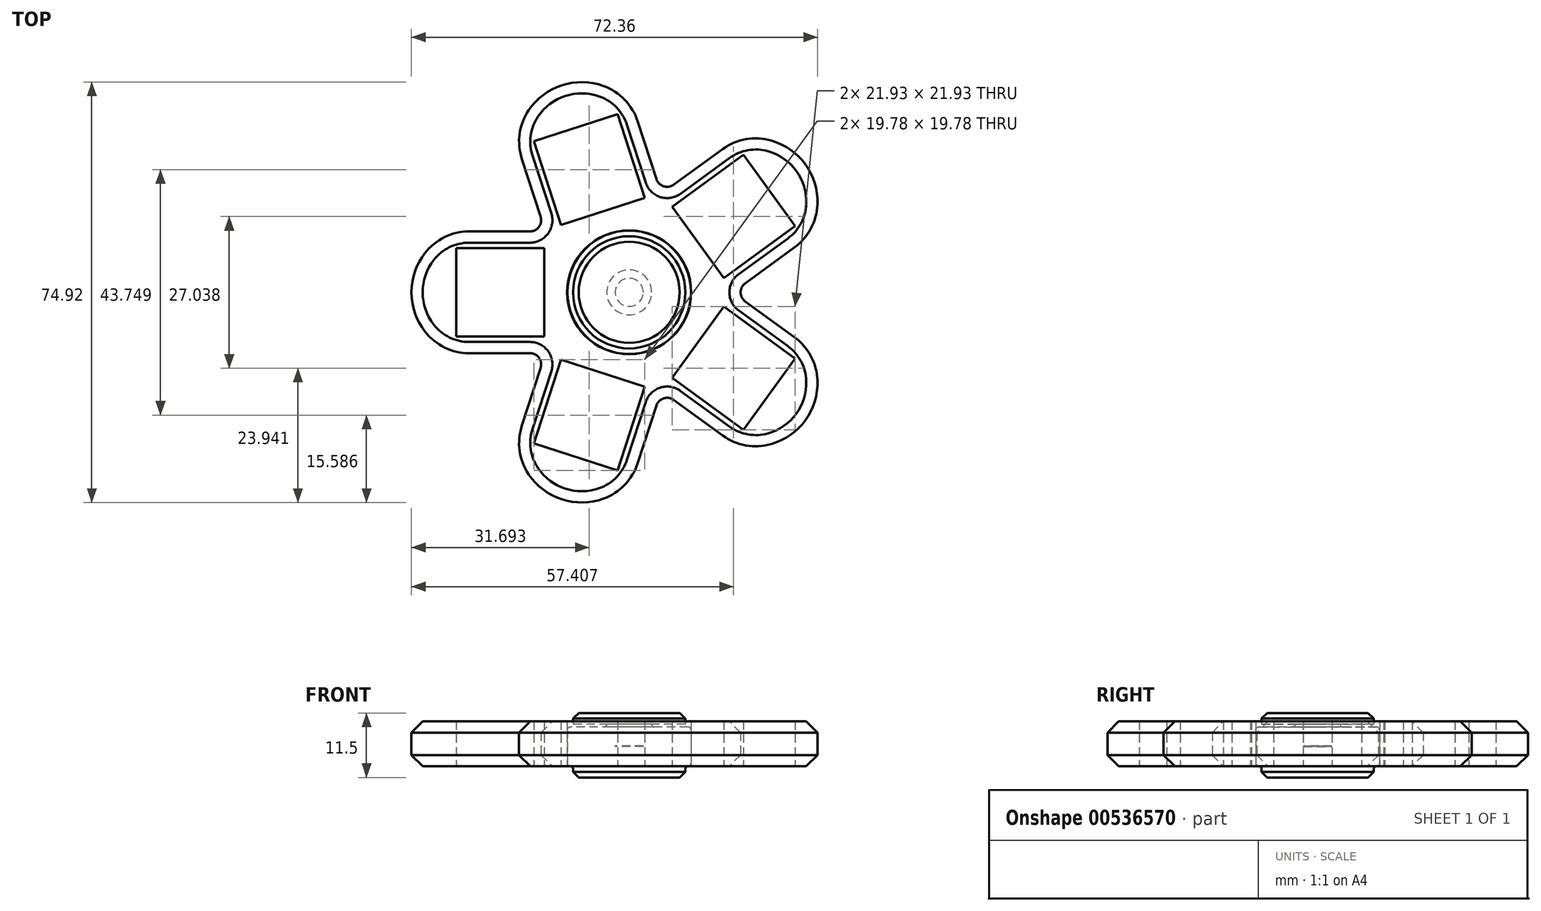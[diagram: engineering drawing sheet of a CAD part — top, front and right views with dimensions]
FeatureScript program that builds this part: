
annotation { "Feature Type Name" : "Feature", "Feature Type Description" : "" }
export const myFeature = defineFeature(function(context is Context, id is Id, definition is map)
    precondition{}
    {
        {
            var Q0;
            Q0=qCreatedBy(makeId("Top.planeOp"),FACE);
            var sketch = newSketch(context, id + "F0", { "sketchPlane" : qUnion([Q0])});
            skCircle(sketch, "E0", {"center": v(0, 0) * mm, "radius": 11 * mm});
            skCircle(sketch, "E1", {"center": v(0, 0) * mm, "radius": 4 * mm});
            skSolve(sketch);
        }
        {
            var Q0;
            Q0=makeQuery(id+"F0.imprint","IMPRINT",FACE,{"disambiguationData":[TD([[makeQuery(id+"F0.imprint","IMPRINT",EDGE,{"derivedFrom":sQuery(id+"F0.wireOp",EDGE,"E0")}),1.0]])]});
            extrude(context, id + "F1", {"entities" : qUnion([Q0]), "depth" : 7 * mm, "offsetDistance" : 25 * mm});
        }
        {
            var Q0;
            Q0=makeQuery(id+"F1.opExtrude","CAP_FACE",FACE,{"disambiguationData":[OSD([sQuery(id+"F0.wireOp",EDGE,"E0"),sQuery(id+"F0.wireOp",EDGE,"E1")])],"isStart":true});
            var sketch = newSketch(context, id + "F2", { "sketchPlane" : qUnion([Q0])});
            skCircle(sketch, "E2.0", {"center": v(0, 0) * mm, "radius": 11.05 * mm});
            skCircle(sketch, "E3.0", {"center": v(0, 0) * mm, "radius": 15.05 * mm});
            skLineSegment(sketch, "E4", {"start": v(0, 0) * mm, "end": v(-23, 0) * mm, "construction": true});
            skLineSegment(sketch, "E5.bottom", {"start": v(-30.85, -7.85) * mm, "end": v(-15.15, -7.85) * mm});
            skLineSegment(sketch, "E5.top", {"start": v(-30.85, 7.85) * mm, "end": v(-15.15, 7.85) * mm});
            skLineSegment(sketch, "E5.left", {"start": v(-30.85, -7.85) * mm, "end": v(-30.85, 7.85) * mm});
            skLineSegment(sketch, "E5.right", {"start": v(-15.15, -7.85) * mm, "end": v(-15.15, 7.85) * mm});
            skPoint(sketch, "E5.middle", {"position": v(-23, 0) * mm});
            skCircle(sketch, "E6", {"center": v(0, 0) * mm, "radius": 50 * mm, "construction": true});
            skLineSegment(sketch, "E7", {"start": v(-23, 0) * mm, "end": v(-38.8, 0) * mm, "construction": true});
            skLineSegment(sketch, "E8", {"start": v(-30.85, 7.85) * mm, "end": v(-30.85, 10.85) * mm, "construction": true});
            skLineSegment(sketch, "E9.0", {"start": v(-23, 10.85) * mm, "end": v(-30.85, 10.85) * mm});
            skLineSegment(sketch, "E9.1", {"start": v(0, 10.85) * mm, "end": v(-2.1, 10.85) * mm, "construction": true});
            skLineSegment(sketch, "E10.trimOffspring", {"start": v(-10.43, 10.85) * mm, "end": v(-23, 10.85) * mm});
            skLineSegment(sketch, "E11.MirrorCS", {"start": v(-10.43, -10.85) * mm, "end": v(-23, -10.85) * mm});
            skLineSegment(sketch, "E12.MirrorCS", {"start": v(-23, -10.85) * mm, "end": v(-30.85, -10.85) * mm});
            skArc(sketch, "E13", {"start": v(-30.85, 10.85) * mm, "mid": v(-38.8, 0) * mm, "end": v(-30.85, -10.85) * mm});
            skLineSegment(sketch, "E14.1.0", {"start": v(-2.07, -31.77) * mm, "end": v(2.78, -16.83) * mm});
            skLineSegment(sketch, "E14.1.1", {"start": v(2.78, -16.83) * mm, "end": v(-12.15, -11.98) * mm});
            skLineSegment(sketch, "E14.1.2", {"start": v(-17, -26.91) * mm, "end": v(-12.15, -11.98) * mm});
            skLineSegment(sketch, "E14.1.3", {"start": v(-13.54, -6.57) * mm, "end": v(-17.43, -18.52) * mm});
            skLineSegment(sketch, "E14.1.4", {"start": v(-17.43, -18.52) * mm, "end": v(-19.85, -25.99) * mm});
            skLineSegment(sketch, "E14.1.5", {"start": v(-2.07, -31.77) * mm, "end": v(-17, -26.91) * mm});
            skArc(sketch, "E14.1.6", {"start": v(-19.85, -25.99) * mm, "mid": v(-11.99, -36.9) * mm, "end": v(0.79, -32.7) * mm});
            skLineSegment(sketch, "E14.1.7", {"start": v(3.21, -25.23) * mm, "end": v(0.79, -32.7) * mm});
            skLineSegment(sketch, "E14.1.8", {"start": v(7.1, -13.27) * mm, "end": v(3.21, -25.23) * mm});
            skLineSegment(sketch, "E14.2.0", {"start": v(29.57, -11.78) * mm, "end": v(16.87, -2.55) * mm});
            skLineSegment(sketch, "E14.2.1", {"start": v(16.87, -2.55) * mm, "end": v(7.64, -15.26) * mm});
            skLineSegment(sketch, "E14.2.2", {"start": v(20.34, -24.48) * mm, "end": v(7.64, -15.26) * mm});
            skLineSegment(sketch, "E14.2.3", {"start": v(2.06, -14.9) * mm, "end": v(12.23, -22.3) * mm});
            skLineSegment(sketch, "E14.2.4", {"start": v(12.23, -22.3) * mm, "end": v(18.58, -26.91) * mm});
            skLineSegment(sketch, "E14.2.5", {"start": v(29.57, -11.78) * mm, "end": v(20.34, -24.48) * mm});
            skArc(sketch, "E14.2.6", {"start": v(18.58, -26.91) * mm, "mid": v(31.39, -22.8) * mm, "end": v(31.34, -9.36) * mm});
            skLineSegment(sketch, "E14.2.7", {"start": v(24.98, -4.74) * mm, "end": v(31.34, -9.36) * mm});
            skLineSegment(sketch, "E14.2.8", {"start": v(14.82, 2.65) * mm, "end": v(24.98, -4.74) * mm});
            skCircle(sketch, "E15", {"center": v(0, 0) * mm, "radius": 32.7 * mm, "construction": true});
            skLineSegment(sketch, "E16.3.3.0", {"start": v(7.64, 15.26) * mm, "end": v(16.87, 2.55) * mm});
            skLineSegment(sketch, "E16.6.3.0", {"start": v(29.57, 11.78) * mm, "end": v(16.87, 2.55) * mm});
            skLineSegment(sketch, "E16.9.3.0", {"start": v(14.82, -2.65) * mm, "end": v(24.98, 4.74) * mm});
            skLineSegment(sketch, "E16.12.3.0", {"start": v(24.98, 4.74) * mm, "end": v(31.34, 9.36) * mm});
            skLineSegment(sketch, "E16.15.3.0", {"start": v(20.34, 24.48) * mm, "end": v(29.57, 11.78) * mm});
            skArc(sketch, "E16.18.3.0", {"start": v(31.34, 9.36) * mm, "mid": v(31.39, 22.8) * mm, "end": v(18.58, 26.91) * mm});
            skLineSegment(sketch, "E16.21.3.0", {"start": v(20.34, 24.48) * mm, "end": v(7.64, 15.26) * mm});
            skLineSegment(sketch, "E16.22.3.0", {"start": v(12.23, 22.3) * mm, "end": v(18.58, 26.91) * mm});
            skLineSegment(sketch, "E16.25.3.0", {"start": v(2.06, 14.9) * mm, "end": v(12.23, 22.3) * mm});
            skLineSegment(sketch, "E16.3.4.0", {"start": v(-12.15, 11.98) * mm, "end": v(2.78, 16.83) * mm});
            skLineSegment(sketch, "E16.6.4.0", {"start": v(-2.07, 31.77) * mm, "end": v(2.78, 16.83) * mm});
            skLineSegment(sketch, "E16.9.4.0", {"start": v(7.1, 13.27) * mm, "end": v(3.21, 25.23) * mm});
            skLineSegment(sketch, "E16.12.4.0", {"start": v(3.21, 25.23) * mm, "end": v(0.79, 32.7) * mm});
            skLineSegment(sketch, "E16.15.4.0", {"start": v(-17, 26.91) * mm, "end": v(-2.07, 31.77) * mm});
            skArc(sketch, "E16.18.4.0", {"start": v(0.79, 32.7) * mm, "mid": v(-11.99, 36.9) * mm, "end": v(-19.85, 25.99) * mm});
            skLineSegment(sketch, "E16.21.4.0", {"start": v(-17, 26.91) * mm, "end": v(-12.15, 11.98) * mm});
            skLineSegment(sketch, "E16.22.4.0", {"start": v(-17.43, 18.52) * mm, "end": v(-19.85, 25.99) * mm});
            skLineSegment(sketch, "E16.25.4.0", {"start": v(-13.54, 6.57) * mm, "end": v(-17.43, 18.52) * mm});
            skSolve(sketch);
        }
        {
            var Q0;
            {var subQ5=sQuery(id+"F2.wireOp",EDGE,"E14.2.0");Q0=makeQuery(id+"F2.imprint","IMPRINT",FACE,{"disambiguationData":[TD([[makeQuery(id+"F2.imprint","IMPRINT",EDGE,{"derivedFrom":subQ5}),-1.0]])]});}
            var Q1;
            {var subQ6=sQuery(id+"F2.wireOp",EDGE,"E14.1.0");Q1=makeQuery(id+"F2.imprint","IMPRINT",FACE,{"disambiguationData":[TD([[makeQuery(id+"F2.imprint","IMPRINT",EDGE,{"derivedFrom":subQ6}),-1.0]])]});}
            var Q2;
            {var subQ5=sQuery(id+"F2.wireOp",EDGE,"E5.bottom");Q2=makeQuery(id+"F2.imprint","IMPRINT",FACE,{"disambiguationData":[TD([[makeQuery(id+"F2.imprint","IMPRINT",EDGE,{"derivedFrom":subQ5}),-1.0]])]});}
            var Q3;
            Q3=makeQuery(id+"F2.imprint","IMPRINT",FACE,{"disambiguationData":[TD([[makeQuery(id+"F2.imprint","IMPRINT",EDGE,{"derivedFrom":sQuery(id+"F2.wireOp",EDGE,"E16.3.4.0")}),-1.0]])]});
            var Q4;
            {var subQ0=sQuery(id+"F2.wireOp",EDGE,"E10.trimOffspring");var subQ1=sQuery(id+"F2.wireOp",EDGE,"E3.0");var subQ2=makeQuery(id+"F2.imprint","INTERSECT",VERTEX,{"derivedFrom":[subQ1,subQ0]});Q4=makeQuery(id+"F2.imprint","IMPRINT",FACE,{"disambiguationData":[TD([[makeQuery(id+"F2.imprint","IMPRINT",EDGE,{"disambiguationData":[TD([[subQ2,-1.0]])],"derivedFrom":subQ1}),-1.0]])]});}
            var Q5;
            Q5=makeQuery(id+"F2.imprint","IMPRINT",FACE,{"disambiguationData":[TD([[makeQuery(id+"F2.imprint","IMPRINT",EDGE,{"derivedFrom":sQuery(id+"F2.wireOp",EDGE,"E16.3.3.0")}),-1.0]])]});
            var Q6;
            {var subQ0=sQuery(id+"F2.wireOp",EDGE,"E16.25.3.0");var subQ1=sQuery(id+"F2.wireOp",EDGE,"E3.0");var subQ2=makeQuery(id+"F2.imprint","INTERSECT",VERTEX,{"derivedFrom":[subQ1,subQ0]});Q6=makeQuery(id+"F2.imprint","IMPRINT",FACE,{"disambiguationData":[TD([[makeQuery(id+"F2.imprint","IMPRINT",EDGE,{"disambiguationData":[TD([[subQ2,1.0]])],"derivedFrom":subQ1}),-1.0]])]});}
            var Q7;
            {var subQ0=sQuery(id+"F2.wireOp",EDGE,"E14.2.8");var subQ1=sQuery(id+"F2.wireOp",EDGE,"E3.0");var subQ2=makeQuery(id+"F2.imprint","INTERSECT",VERTEX,{"derivedFrom":[subQ1,subQ0]});Q7=makeQuery(id+"F2.imprint","IMPRINT",FACE,{"disambiguationData":[TD([[makeQuery(id+"F2.imprint","IMPRINT",EDGE,{"disambiguationData":[TD([[subQ2,1.0]])],"derivedFrom":subQ1}),-1.0]])]});}
            var Q8;
            {var subQ0=sQuery(id+"F2.wireOp",EDGE,"E11.MirrorCS");var subQ1=sQuery(id+"F2.wireOp",EDGE,"E3.0");var subQ2=makeQuery(id+"F2.imprint","INTERSECT",VERTEX,{"derivedFrom":[subQ1,subQ0]});Q8=makeQuery(id+"F2.imprint","IMPRINT",FACE,{"disambiguationData":[TD([[makeQuery(id+"F2.imprint","IMPRINT",EDGE,{"disambiguationData":[TD([[subQ2,1.0]])],"derivedFrom":subQ1}),-1.0]])]});}
            var Q9;
            Q9=makeQuery(id+"F2.imprint","IMPRINT",FACE,{"disambiguationData":[TD([[makeQuery(id+"F2.imprint","IMPRINT",EDGE,{"derivedFrom":sQuery(id+"F2.wireOp",EDGE,"E2.0")}),-1.0]])]});
            var Q10;
            {var subQ0=sQuery(id+"F2.wireOp",EDGE,"E14.1.8");var subQ1=sQuery(id+"F2.wireOp",EDGE,"E3.0");var subQ2=makeQuery(id+"F2.imprint","INTERSECT",VERTEX,{"derivedFrom":[subQ1,subQ0]});Q10=makeQuery(id+"F2.imprint","IMPRINT",FACE,{"disambiguationData":[TD([[makeQuery(id+"F2.imprint","IMPRINT",EDGE,{"disambiguationData":[TD([[subQ2,1.0]])],"derivedFrom":subQ1}),-1.0]])]});}
            extrude(context, id + "F3", {"entities" : qUnion([Q0, Q1, Q2, Q3, Q4, Q5, Q6, Q7, Q8, Q9, Q10]), "oppositeDirection" : true, "depth" : 8 * mm, "offsetDistance" : 25 * mm});
        }
        {
            var Q0;
            Q0=makeQuery(id+"F3.opExtrude","SWEPT_EDGE",EDGE,{"disambiguationData":[OSD([sQuery(id+"F2.wireOp",EDGE,"E3.0"),sQuery(id+"F2.wireOp",EDGE,"E14.2.3")])]});
            var Q1;
            Q1=makeQuery(id+"F3.opExtrude","SWEPT_EDGE",EDGE,{"disambiguationData":[OSD([sQuery(id+"F2.wireOp",EDGE,"E3.0"),sQuery(id+"F2.wireOp",EDGE,"E14.1.8")])]});
            var Q2;
            Q2=makeQuery(id+"F3.opExtrude","SWEPT_EDGE",EDGE,{"disambiguationData":[OSD([sQuery(id+"F2.wireOp",EDGE,"E3.0"),sQuery(id+"F2.wireOp",EDGE,"E14.2.8")])]});
            var Q3;
            Q3=makeQuery(id+"F3.opExtrude","SWEPT_EDGE",EDGE,{"disambiguationData":[OSD([sQuery(id+"F2.wireOp",EDGE,"E3.0"),sQuery(id+"F2.wireOp",EDGE,"E10.trimOffspring")])]});
            var Q4;
            Q4=makeQuery(id+"F3.opExtrude","SWEPT_EDGE",EDGE,{"disambiguationData":[OSD([sQuery(id+"F2.wireOp",EDGE,"E3.0"),sQuery(id+"F2.wireOp",EDGE,"E11.MirrorCS")])]});
            var Q5;
            Q5=makeQuery(id+"F3.opExtrude","SWEPT_EDGE",EDGE,{"disambiguationData":[OSD([sQuery(id+"F2.wireOp",EDGE,"E3.0"),sQuery(id+"F2.wireOp",EDGE,"E14.1.3")])]});
            var Q6;
            Q6=makeQuery(id+"F3.opExtrude","SWEPT_EDGE",EDGE,{"disambiguationData":[OSD([sQuery(id+"F2.wireOp",EDGE,"E16.25.3.0"),sQuery(id+"F2.wireOp",EDGE,"E16.9.4.0")])]});
            fillet(context, id + "F4", {"entities" : qUnion([Q0, Q1, Q2, Q3, Q4, Q5, Q6]), "radius" : 2 * mm, "tangentPropagation" : true, "allowEdgeOverflow" : false});
        }
        {
            var Q0;
            Q0=makeQuery(id+"F3.opExtrude","SWEPT_EDGE",EDGE,{"disambiguationData":[OSD([sQuery(id+"F2.wireOp",EDGE,"E14.2.4"),sQuery(id+"F2.wireOp",EDGE,"E14.2.6")])]});
            var Q1;
            Q1=makeQuery(id+"F3.opExtrude","SWEPT_EDGE",EDGE,{"disambiguationData":[OSD([sQuery(id+"F2.wireOp",EDGE,"E14.2.6"),sQuery(id+"F2.wireOp",EDGE,"E14.2.7")])]});
            var Q2;
            Q2=makeQuery(id+"F3.opExtrude","SWEPT_EDGE",EDGE,{"disambiguationData":[OSD([sQuery(id+"F2.wireOp",EDGE,"E9.0"),sQuery(id+"F2.wireOp",EDGE,"E13")])]});
            var Q3;
            Q3=makeQuery(id+"F3.opExtrude","SWEPT_EDGE",EDGE,{"disambiguationData":[OSD([sQuery(id+"F2.wireOp",EDGE,"E12.MirrorCS"),sQuery(id+"F2.wireOp",EDGE,"E13")])]});
            var Q4;
            Q4=makeQuery(id+"F3.opExtrude","SWEPT_EDGE",EDGE,{"disambiguationData":[OSD([sQuery(id+"F2.wireOp",EDGE,"E14.1.4"),sQuery(id+"F2.wireOp",EDGE,"E14.1.6")])]});
            var Q5;
            Q5=makeQuery(id+"F3.opExtrude","SWEPT_EDGE",EDGE,{"disambiguationData":[OSD([sQuery(id+"F2.wireOp",EDGE,"E14.1.6"),sQuery(id+"F2.wireOp",EDGE,"E14.1.7")])]});
            var Q6;
            Q6=makeQuery(id+"F3.opExtrude","SWEPT_EDGE",EDGE,{"disambiguationData":[OSD([sQuery(id+"F2.wireOp",EDGE,"E16.18.4.0"),sQuery(id+"F2.wireOp",EDGE,"E16.22.4.0")])]});
            var Q7;
            Q7=makeQuery(id+"F3.opExtrude","SWEPT_EDGE",EDGE,{"disambiguationData":[OSD([sQuery(id+"F2.wireOp",EDGE,"E16.12.4.0"),sQuery(id+"F2.wireOp",EDGE,"E16.18.4.0")])]});
            var Q8;
            Q8=makeQuery(id+"F3.opExtrude","SWEPT_EDGE",EDGE,{"disambiguationData":[OSD([sQuery(id+"F2.wireOp",EDGE,"E16.18.3.0"),sQuery(id+"F2.wireOp",EDGE,"E16.22.3.0")])]});
            var Q9;
            Q9=makeQuery(id+"F3.opExtrude","SWEPT_EDGE",EDGE,{"disambiguationData":[OSD([sQuery(id+"F2.wireOp",EDGE,"E16.12.3.0"),sQuery(id+"F2.wireOp",EDGE,"E16.18.3.0")])]});
            fillet(context, id + "F5", {"entities" : qUnion([Q0, Q1, Q2, Q3, Q4, Q5, Q6, Q7, Q8, Q9]), "radius" : 10 * mm, "tangentPropagation" : true, "allowEdgeOverflow" : false});
        }
        {
            var Q0;
            Q0=makeQuery(id+"F3.opExtrude","CAP_EDGE",EDGE,{"disambiguationData":[OSD([sQuery(id+"F2.wireOp",EDGE,"E14.2.6")])],"isStart":false});
            var Q1;
            Q1=makeQuery(id+"F3.opExtrude","CAP_EDGE",EDGE,{"disambiguationData":[OSD([sQuery(id+"F2.wireOp",EDGE,"E14.1.6")])],"isStart":false});
            var Q2;
            {var subQ0=sQuery(id+"F2.wireOp",EDGE,"E13");var subQ1=sQuery(id+"F2.wireOp",EDGE,"E9.0");Q2=makeQuery(id+"F5.opFillet","BLEND_EDGE",EDGE,{"blendedFrom":[makeQuery(id+"F3.opExtrude","SWEPT_EDGE",EDGE,{"disambiguationData":[OSD([subQ1,subQ0])]}),makeQuery(id+"F3.opExtrude","CAP_FACE",FACE,{"disambiguationData":[OSD([sQuery(id+"F2.wireOp",EDGE,"E2.0"),sQuery(id+"F2.wireOp",EDGE,"E3.0"),sQuery(id+"F2.wireOp",EDGE,"E5.bottom"),sQuery(id+"F2.wireOp",EDGE,"E5.top"),sQuery(id+"F2.wireOp",EDGE,"E5.left"),sQuery(id+"F2.wireOp",EDGE,"E5.right"),subQ1,sQuery(id+"F2.wireOp",EDGE,"E10.trimOffspring"),sQuery(id+"F2.wireOp",EDGE,"E11.MirrorCS"),sQuery(id+"F2.wireOp",EDGE,"E12.MirrorCS"),subQ0,sQuery(id+"F2.wireOp",EDGE,"E14.1.0"),sQuery(id+"F2.wireOp",EDGE,"E14.1.1"),sQuery(id+"F2.wireOp",EDGE,"E14.1.2"),sQuery(id+"F2.wireOp",EDGE,"E14.1.3"),sQuery(id+"F2.wireOp",EDGE,"E14.1.4"),sQuery(id+"F2.wireOp",EDGE,"E14.1.5"),sQuery(id+"F2.wireOp",EDGE,"E14.1.6"),sQuery(id+"F2.wireOp",EDGE,"E14.1.7"),sQuery(id+"F2.wireOp",EDGE,"E14.1.8"),sQuery(id+"F2.wireOp",EDGE,"E14.2.0"),sQuery(id+"F2.wireOp",EDGE,"E14.2.1"),sQuery(id+"F2.wireOp",EDGE,"E14.2.2"),sQuery(id+"F2.wireOp",EDGE,"E14.2.3"),sQuery(id+"F2.wireOp",EDGE,"E14.2.4"),sQuery(id+"F2.wireOp",EDGE,"E14.2.5"),sQuery(id+"F2.wireOp",EDGE,"E14.2.6"),sQuery(id+"F2.wireOp",EDGE,"E14.2.7"),sQuery(id+"F2.wireOp",EDGE,"E14.2.8")])],"isStart":false})],"blendedInto":[makeQuery(id+"F3.opExtrude","CAP_FACE",FACE,{"disambiguationData":[OSD([sQuery(id+"F2.wireOp",EDGE,"E2.0"),sQuery(id+"F2.wireOp",EDGE,"E3.0"),sQuery(id+"F2.wireOp",EDGE,"E5.bottom"),sQuery(id+"F2.wireOp",EDGE,"E5.top"),sQuery(id+"F2.wireOp",EDGE,"E5.left"),sQuery(id+"F2.wireOp",EDGE,"E5.right"),subQ1,sQuery(id+"F2.wireOp",EDGE,"E10.trimOffspring"),sQuery(id+"F2.wireOp",EDGE,"E11.MirrorCS"),sQuery(id+"F2.wireOp",EDGE,"E12.MirrorCS"),subQ0,sQuery(id+"F2.wireOp",EDGE,"E14.1.0"),sQuery(id+"F2.wireOp",EDGE,"E14.1.1"),sQuery(id+"F2.wireOp",EDGE,"E14.1.2"),sQuery(id+"F2.wireOp",EDGE,"E14.1.3"),sQuery(id+"F2.wireOp",EDGE,"E14.1.4"),sQuery(id+"F2.wireOp",EDGE,"E14.1.5"),sQuery(id+"F2.wireOp",EDGE,"E14.1.6"),sQuery(id+"F2.wireOp",EDGE,"E14.1.7"),sQuery(id+"F2.wireOp",EDGE,"E14.1.8"),sQuery(id+"F2.wireOp",EDGE,"E14.2.0"),sQuery(id+"F2.wireOp",EDGE,"E14.2.1"),sQuery(id+"F2.wireOp",EDGE,"E14.2.2"),sQuery(id+"F2.wireOp",EDGE,"E14.2.3"),sQuery(id+"F2.wireOp",EDGE,"E14.2.4"),sQuery(id+"F2.wireOp",EDGE,"E14.2.5"),sQuery(id+"F2.wireOp",EDGE,"E14.2.6"),sQuery(id+"F2.wireOp",EDGE,"E14.2.7"),sQuery(id+"F2.wireOp",EDGE,"E14.2.8")])],"isStart":false})]});}
            var Q3;
            Q3=makeQuery(id+"F3.opExtrude","CAP_EDGE",EDGE,{"disambiguationData":[OSD([sQuery(id+"F2.wireOp",EDGE,"E14.2.6")])],"isStart":true});
            var Q4;
            Q4=makeQuery(id+"F3.opExtrude","CAP_EDGE",EDGE,{"disambiguationData":[OSD([sQuery(id+"F2.wireOp",EDGE,"E13")])],"isStart":true});
            var Q5;
            Q5=makeQuery(id+"F3.opExtrude","CAP_EDGE",EDGE,{"disambiguationData":[OSD([sQuery(id+"F2.wireOp",EDGE,"E14.1.6")])],"isStart":true});
            chamfer(context, id + "F6", {"entities" : qUnion([Q0, Q1, Q2, Q3, Q4, Q5]), "width" : 2 * mm, "tangentPropagation" : true});
        }
        {
            var Q0;
            Q0=makeQuery(id+"F3.opExtrude","CAP_FACE",FACE,{"disambiguationData":[OSD([sQuery(id+"F2.wireOp",EDGE,"E2.0"),sQuery(id+"F2.wireOp",EDGE,"E3.0"),sQuery(id+"F2.wireOp",EDGE,"E5.bottom"),sQuery(id+"F2.wireOp",EDGE,"E5.top"),sQuery(id+"F2.wireOp",EDGE,"E5.left"),sQuery(id+"F2.wireOp",EDGE,"E5.right"),sQuery(id+"F2.wireOp",EDGE,"E9.0"),sQuery(id+"F2.wireOp",EDGE,"E10.trimOffspring"),sQuery(id+"F2.wireOp",EDGE,"E11.MirrorCS"),sQuery(id+"F2.wireOp",EDGE,"E12.MirrorCS"),sQuery(id+"F2.wireOp",EDGE,"E13"),sQuery(id+"F2.wireOp",EDGE,"E14.1.0"),sQuery(id+"F2.wireOp",EDGE,"E14.1.1"),sQuery(id+"F2.wireOp",EDGE,"E14.1.2"),sQuery(id+"F2.wireOp",EDGE,"E14.1.3"),sQuery(id+"F2.wireOp",EDGE,"E14.1.4"),sQuery(id+"F2.wireOp",EDGE,"E14.1.5"),sQuery(id+"F2.wireOp",EDGE,"E14.1.6"),sQuery(id+"F2.wireOp",EDGE,"E14.1.7"),sQuery(id+"F2.wireOp",EDGE,"E14.1.8"),sQuery(id+"F2.wireOp",EDGE,"E14.2.0"),sQuery(id+"F2.wireOp",EDGE,"E14.2.1"),sQuery(id+"F2.wireOp",EDGE,"E14.2.2"),sQuery(id+"F2.wireOp",EDGE,"E14.2.3"),sQuery(id+"F2.wireOp",EDGE,"E14.2.4"),sQuery(id+"F2.wireOp",EDGE,"E14.2.5"),sQuery(id+"F2.wireOp",EDGE,"E14.2.6"),sQuery(id+"F2.wireOp",EDGE,"E14.2.7"),sQuery(id+"F2.wireOp",EDGE,"E14.2.8")])],"isStart":true});
            var sketch = newSketch(context, id + "F7", { "sketchPlane" : qUnion([Q0])});
            skLineSegment(sketch, "E17.0", {"start": v(-4.57, -33.06) * mm, "end": v(-15.73, -29.43) * mm});
            skArc(sketch, "E18.0", {"start": v(-5.26, -34.89) * mm, "mid": v(-11.7, -34.47) * mm, "end": v(-15.73, -29.43) * mm});
            skArc(sketch, "E18.1", {"start": v(-16.25, -31.32) * mm, "mid": v(-11.37, -35) * mm, "end": v(-5.26, -34.89) * mm});
            skArc(sketch, "E18.2", {"start": v(-4.57, -33.06) * mm, "mid": v(-10.8, -34.76) * mm, "end": v(-16.25, -31.32) * mm});
            skArc(sketch, "E19.0", {"start": v(31.56, -15.78) * mm, "mid": v(29.17, -21.78) * mm, "end": v(23.13, -24.06) * mm});
            skArc(sketch, "E19.1", {"start": v(24.76, -25.14) * mm, "mid": v(29.77, -21.63) * mm, "end": v(31.56, -15.78) * mm});
            skArc(sketch, "E19.2", {"start": v(30.03, -14.56) * mm, "mid": v(29.72, -21) * mm, "end": v(24.76, -25.14) * mm});
            skLineSegment(sketch, "E20.0", {"start": v(30.03, -14.56) * mm, "end": v(23.13, -24.06) * mm});
            skArc(sketch, "E21.0", {"start": v(-34.8, -5.78) * mm, "mid": v(-33.9, -6.76) * mm, "end": v(-32.85, -7.57) * mm});
            skArc(sketch, "E21.1", {"start": v(-34.8, 5.78) * mm, "mid": v(-36.8, 0) * mm, "end": v(-34.8, -5.78) * mm});
            skArc(sketch, "E21.2", {"start": v(-32.85, 7.57) * mm, "mid": v(-33.9, 6.76) * mm, "end": v(-34.8, 5.78) * mm});
            skLineSegment(sketch, "E22.0", {"start": v(-32.85, -7.57) * mm, "end": v(-32.85, 7.57) * mm});
            skSolve(sketch);
        }
        {
            var Q0;
            Q0=makeQuery(id+"F1.opExtrude","CAP_FACE",FACE,{"disambiguationData":[OSD([sQuery(id+"F0.wireOp",EDGE,"E0"),sQuery(id+"F0.wireOp",EDGE,"E1")])],"isStart":true});
            var sketch = newSketch(context, id + "F8", { "sketchPlane" : qUnion([Q0])});
            skCircle(sketch, "E23.0", {"center": v(0, 0) * mm, "radius": 10 * mm});
            skSolve(sketch);
        }
        {
            var Q0;
            Q0=makeQuery(id+"F8.imprint","IMPRINT",FACE,{"disambiguationData":[TD([[makeQuery(id+"F8.imprint","IMPRINT",EDGE,{"derivedFrom":sQuery(id+"F8.wireOp",EDGE,"E23.0")}),1.0]])]});
            var Q1;
            Q1=makeQuery(id+"F8.imprint","IMPRINT",FACE,{"disambiguationData":[TD([[makeQuery(id+"F8.imprint","IMPRINT",EDGE,{"derivedFrom":sQuery(id+"F8.wireOp",EDGE,"c407c948-2510-426a-b12c-06ac0bc9cf64.0")}),-1.0]])]});
            var Q2;
            Q2=makeQuery(id+"F8.imprint","IMPRINT",FACE,{"disambiguationData":[TD([[makeQuery(id+"F8.imprint","IMPRINT",EDGE,{"derivedFrom":sQuery(id+"F8.wireOp",EDGE,"c407c948-2510-426a-b12c-06ac0bc9cf64.0")}),1.0]])]});
            var Q3;
            Q3=makeQuery(id+"F8.imprint","IMPRINT",FACE,{"disambiguationData":[TD([[makeQuery(id+"F8.imprint","IMPRINT",EDGE,{"derivedFrom":makeQuery(id+"F1.opExtrude","CAP_EDGE",EDGE,{"disambiguationData":[OSD([sQuery(id+"F0.wireOp",EDGE,"E1")])],"isStart":true})}),-1.0]])]});
            extrude(context, id + "F9", {"entities" : qUnion([Q0, Q1, Q2, Q3]), "depth" : 2 * mm, "offsetDistance" : 25 * mm});
        }
        {
            var Q0;
            Q0=makeQuery(id+"F8.imprint","IMPRINT",FACE,{"disambiguationData":[TD([[makeQuery(id+"F8.imprint","IMPRINT",EDGE,{"derivedFrom":makeQuery(id+"F1.opExtrude","CAP_EDGE",EDGE,{"disambiguationData":[OSD([sQuery(id+"F0.wireOp",EDGE,"E1")])],"isStart":true})}),-1.0]])]});
            extrude(context, id + "F10", {"entities" : qUnion([Q0]), "operationType" : NewBodyOperationType.ADD, "oppositeDirection" : true, "depth" : 7.5 * mm, "offsetDistance" : 25 * mm});
        }
        {
            var Q0;
            Q0=makeQuery(id+"F10.opExtrude","CAP_FACE",FACE,{"disambiguationData":[OSD([sQuery(id+"F0.wireOp",EDGE,"E1")])],"isStart":false});
            var sketch = newSketch(context, id + "F11", { "sketchPlane" : qUnion([Q0])});
            skCircle(sketch, "E24.0", {"center": v(0, 0) * mm, "radius": 10 * mm});
            skCircle(sketch, "E25.0", {"center": v(0, 0) * mm, "radius": 2.5 * mm});
            skSolve(sketch);
        }
        {
            var Q0;
            Q0=makeQuery(id+"F11.imprint","IMPRINT",FACE,{"disambiguationData":[TD([[makeQuery(id+"F11.imprint","IMPRINT",EDGE,{"derivedFrom":sQuery(id+"F11.wireOp",EDGE,"E25.0")}),1.0]])]});
            extrude(context, id + "F12", {"entities" : qUnion([Q0]), "operationType" : NewBodyOperationType.REMOVE, "oppositeDirection" : true, "depth" : 4 * mm, "offsetDistance" : 25 * mm});
        }
        {
            var Q0;
            Q0=makeQuery(id+"F11.imprint","IMPRINT",FACE,{"disambiguationData":[TD([[makeQuery(id+"F11.imprint","IMPRINT",EDGE,{"derivedFrom":sQuery(id+"F11.wireOp",EDGE,"E24.0")}),1.0]])]});
            var Q1;
            Q1=makeQuery(id+"F11.imprint","IMPRINT",FACE,{"disambiguationData":[TD([[makeQuery(id+"F11.imprint","IMPRINT",EDGE,{"derivedFrom":sQuery(id+"F11.wireOp",EDGE,"a1f51509-8c7b-4646-a507-0ed3af852b90.0")}),-1.0]])]});
            var Q2;
            Q2=makeQuery(id+"F11.imprint","IMPRINT",FACE,{"disambiguationData":[TD([[makeQuery(id+"F11.imprint","IMPRINT",EDGE,{"derivedFrom":sQuery(id+"F11.wireOp",EDGE,"15deca98-b56f-4649-b585-fda4b9412a6e.0")}),1.0]])]});
            var Q3;
            Q3=makeQuery(id+"F11.imprint","IMPRINT",FACE,{"disambiguationData":[TD([[makeQuery(id+"F11.imprint","IMPRINT",EDGE,{"derivedFrom":sQuery(id+"F11.wireOp",EDGE,"a1f51509-8c7b-4646-a507-0ed3af852b90.0")}),1.0]])]});
            var Q4;
            Q4=makeQuery(id+"F11.imprint","IMPRINT",FACE,{"disambiguationData":[TD([[makeQuery(id+"F11.imprint","IMPRINT",EDGE,{"derivedFrom":sQuery(id+"F11.wireOp",EDGE,"E25.0")}),-1.0]])]});
            var Q5;
            Q5=makeQuery(id+"F11.imprint","IMPRINT",FACE,{"disambiguationData":[TD([[makeQuery(id+"F11.imprint","IMPRINT",EDGE,{"derivedFrom":sQuery(id+"F11.wireOp",EDGE,"E25.0")}),1.0]])]});
            extrude(context, id + "F13", {"entities" : qUnion([Q0, Q1, Q2, Q3, Q4, Q5]), "depth" : 2 * mm, "offsetDistance" : 25 * mm});
        }
        {
            var Q0;
            Q0=makeQuery(id+"F11.imprint","IMPRINT",FACE,{"disambiguationData":[TD([[makeQuery(id+"F11.imprint","IMPRINT",EDGE,{"derivedFrom":sQuery(id+"F11.wireOp",EDGE,"E25.0")}),1.0]])]});
            extrude(context, id + "F14", {"entities" : qUnion([Q0]), "operationType" : NewBodyOperationType.ADD, "oppositeDirection" : true, "depth" : 3.9 * mm, "offsetDistance" : 25 * mm});
        }
        {
            var Q0;
            Q0=makeQuery(id+"F9.opExtrude","CAP_FACE",FACE,{"disambiguationData":[OSD([sQuery(id+"F8.wireOp",EDGE,"E23.0")])],"isStart":false});
            var Q1;
            Q1=makeQuery(id+"F13.opExtrude","CAP_EDGE",EDGE,{"disambiguationData":[OSD([sQuery(id+"F11.wireOp",EDGE,"E24.0")])],"isStart":false});
            chamfer(context, id + "F15", {"entities" : qUnion([Q0, Q1]), "width" : 1 * mm, "tangentPropagation" : true});
        }
        {
            var Q0;
            Q0=makeQuery(id+"F1.opExtrude","CAP_FACE",FACE,{"disambiguationData":[OSD([sQuery(id+"F0.wireOp",EDGE,"E0"),sQuery(id+"F0.wireOp",EDGE,"E1")])],"isStart":true});
            var Q1;
            Q1=makeQuery(id+"F1.opExtrude","CAP_FACE",FACE,{"disambiguationData":[OSD([sQuery(id+"F0.wireOp",EDGE,"E0"),sQuery(id+"F0.wireOp",EDGE,"E1")])],"isStart":false});
            fillet(context, id + "F16", {"entities" : qUnion([Q0, Q1]), "radius" : .5 * mm, "tangentPropagation" : true, "allowEdgeOverflow" : false});
        }
    });
